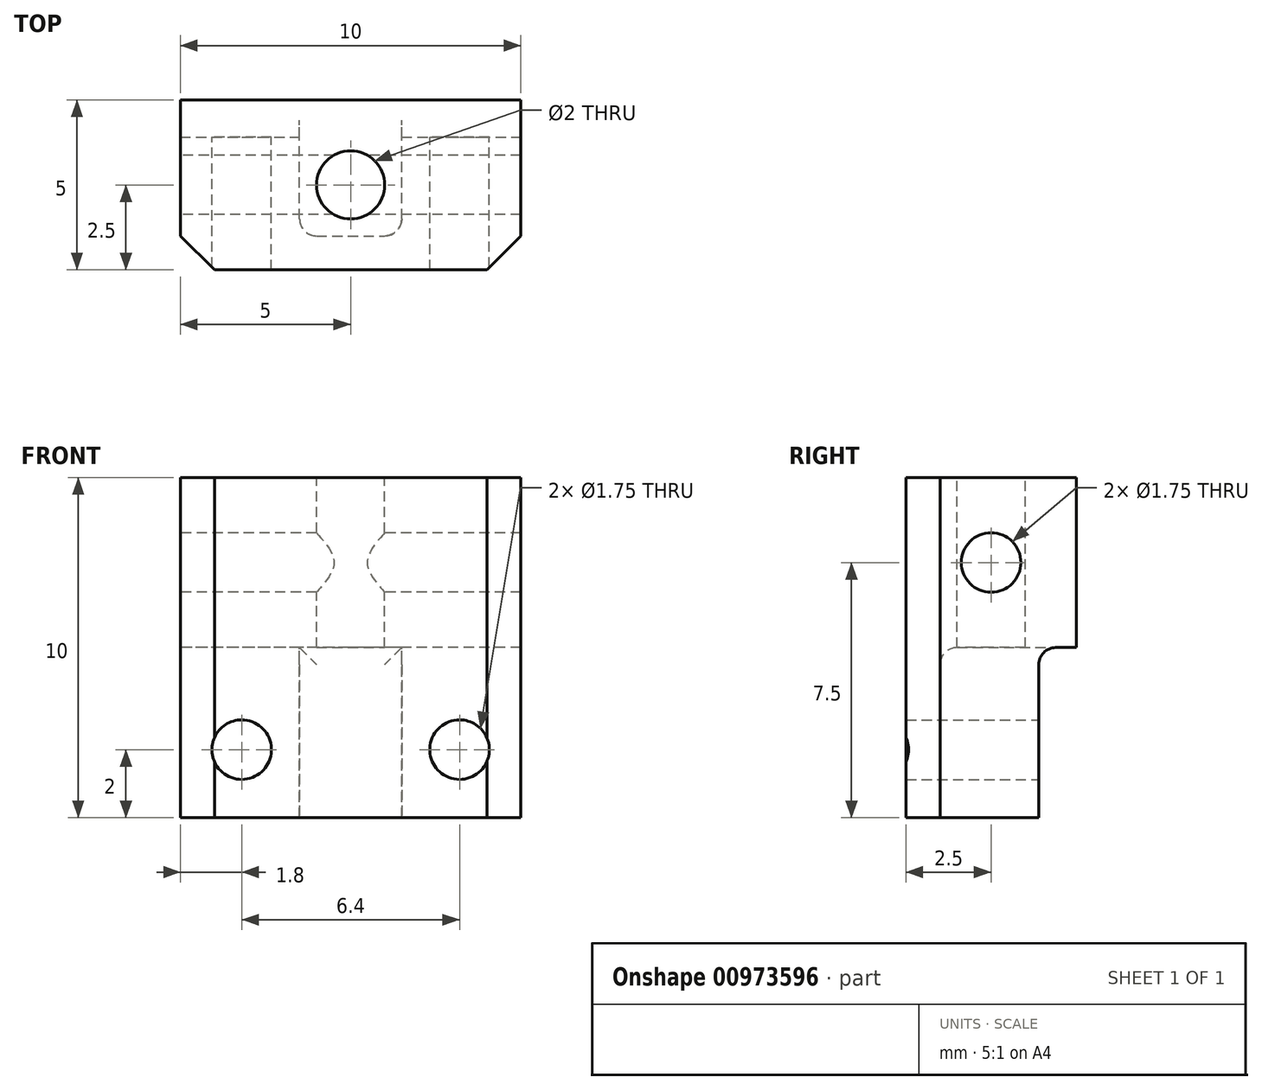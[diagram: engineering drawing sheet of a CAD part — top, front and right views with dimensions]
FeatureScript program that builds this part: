
annotation { "Feature Type Name" : "Feature", "Feature Type Description" : "" }
export const myFeature = defineFeature(function(context is Context, id is Id, definition is map)
    precondition{}
    {
        {
            var Q0;
            Q0=qCreatedBy(makeId("Top.planeOp"),FACE);
            var sketch = newSketch(context, id + "F0", { "sketchPlane" : qUnion([Q0])});
            skLineSegment(sketch, "E0.bottom", {"start": v(-5, 2.5) * mm, "end": v(5, 2.5) * mm});
            skLineSegment(sketch, "E0.top", {"start": v(-5, -2.5) * mm, "end": v(5, -2.5) * mm});
            skLineSegment(sketch, "E0.left", {"start": v(-5, 2.5) * mm, "end": v(-5, -2.5) * mm});
            skLineSegment(sketch, "E0.right", {"start": v(5, 2.5) * mm, "end": v(5, -2.5) * mm});
            skLineSegment(sketch, "E1", {"start": v(0, 65.84) * mm, "end": v(0, -65.84) * mm, "construction": true});
            skLineSegment(sketch, "E2", {"start": v(-87.05, 0) * mm, "end": v(87.05, 0) * mm, "construction": true});
            skSolve(sketch);
        }
        {
            var Q0;
            Q0 = qSketchRegion(id + "F0", true);
            extrude(context, id + "F1", {"entities" : qUnion([Q0]), "depth" : 10 * mm, "offsetDistance" : 25 * mm});
        }
        {
            var Q0;
            Q0=makeQuery(id+"F1.opExtrude","SWEPT_FACE",FACE,{"disambiguationData":[OSD([sQuery(id+"F0.wireOp",EDGE,"E0.bottom")])]});
            var sketch = newSketch(context, id + "F2", { "sketchPlane" : qUnion([Q0])});
            skLineSegment(sketch, "E3.bottom", {"start": v(-1.5, 0) * mm, "end": v(1.5, 0) * mm});
            skLineSegment(sketch, "E3.top", {"start": v(-1.5, 5) * mm, "end": v(1.5, 5) * mm});
            skLineSegment(sketch, "E3.left", {"start": v(-1.5, 0) * mm, "end": v(-1.5, 5) * mm});
            skLineSegment(sketch, "E3.right", {"start": v(1.5, 0) * mm, "end": v(1.5, 5) * mm});
            skLineSegment(sketch, "E4", {"start": v(0, -0.33) * mm, "end": v(0, 10.8) * mm, "construction": true});
            skSolve(sketch);
        }
        {
            var Q0;
            Q0 = qSketchRegion(id + "F2", true);
            extrude(context, id + "F3", {"entities" : qUnion([Q0]), "operationType" : NewBodyOperationType.REMOVE, "oppositeDirection" : true, "depth" : 4 * mm, "offsetDistance" : 25 * mm});
        }
        {
            var Q0;
            Q0=makeQuery(id+"F1.opExtrude","SWEPT_FACE",FACE,{"disambiguationData":[OSD([sQuery(id+"F0.wireOp",EDGE,"E0.bottom")])]});
            var sketch = newSketch(context, id + "F4", { "sketchPlane" : qUnion([Q0])});
            skLineSegment(sketch, "E5.bottom", {"start": v(-5, 0) * mm, "end": v(5, 0) * mm});
            skLineSegment(sketch, "E5.top", {"start": v(-5, 5) * mm, "end": v(5, 5) * mm});
            skLineSegment(sketch, "E5.left", {"start": v(-5, 0) * mm, "end": v(-5, 5) * mm});
            skLineSegment(sketch, "E5.right", {"start": v(5, 0) * mm, "end": v(5, 5) * mm});
            skSolve(sketch);
        }
        {
            var Q0;
            Q0 = qSketchRegion(id + "F4", true);
            extrude(context, id + "F5", {"entities" : qUnion([Q0]), "operationType" : NewBodyOperationType.REMOVE, "oppositeDirection" : true, "depth" : 1.1 * mm, "offsetDistance" : 25 * mm});
        }
        {
            var Q0;
            Q0=makeQuery(id+"F3.boolean.opBoolean","COPY",EDGE,{"derivedFrom":makeQuery(id+"F3.opExtrude","CAP_EDGE",EDGE,{"disambiguationData":[OSD([sQuery(id+"F2.wireOp",EDGE,"E3.left")])],"isStart":false})});
            var Q1;
            Q1=makeQuery(id+"F3.boolean.opBoolean","COPY",EDGE,{"derivedFrom":makeQuery(id+"F3.opExtrude","CAP_EDGE",EDGE,{"disambiguationData":[OSD([sQuery(id+"F2.wireOp",EDGE,"E3.right")])],"isStart":false})});
            var Q2;
            Q2=makeQuery(id+"F3.boolean.opBoolean","COPY",EDGE,{"derivedFrom":makeQuery(id+"F3.opExtrude","CAP_EDGE",EDGE,{"disambiguationData":[OSD([sQuery(id+"F2.wireOp",EDGE,"E3.top")])],"isStart":false})});
            fillet(context, id + "F6", {"entities" : qUnion([Q0, Q1, Q2]), "radius" : 0.5 * mm, "tangentPropagation" : true, "allowEdgeOverflow" : false});
        }
        {
            var Q0;
            {var subQ0=sQuery(id+"F4.wireOp",EDGE,"E5.top");Q0=makeQuery(id+"F5.boolean.opBoolean","COPY",EDGE,{"disambiguationData":[TD([makeQuery(id+"F1.opExtrude","SWEPT_FACE",FACE,{"disambiguationData":[OSD([sQuery(id+"F0.wireOp",EDGE,"E0.left")])]})])],"derivedFrom":makeQuery(id+"F5.opExtrude","CAP_EDGE",EDGE,{"disambiguationData":[OSD([subQ0])],"isStart":false})});}
            var Q1;
            {var subQ0=sQuery(id+"F4.wireOp",EDGE,"E5.top");Q1=makeQuery(id+"F5.boolean.opBoolean","COPY",EDGE,{"disambiguationData":[TD([makeQuery(id+"F1.opExtrude","SWEPT_FACE",FACE,{"disambiguationData":[OSD([sQuery(id+"F0.wireOp",EDGE,"E0.right")])]})])],"derivedFrom":makeQuery(id+"F5.opExtrude","CAP_EDGE",EDGE,{"disambiguationData":[OSD([subQ0])],"isStart":false})});}
            fillet(context, id + "F7", {"entities" : qUnion([Q0, Q1]), "radius" : 0.5 * mm, "tangentPropagation" : true, "allowEdgeOverflow" : false});
        }
        {
            var Q0;
            Q0=makeQuery(id+"F1.opExtrude","SWEPT_EDGE",EDGE,{"disambiguationData":[OSD([sQuery(id+"F0.wireOp",EDGE,"E0.top"),sQuery(id+"F0.wireOp",EDGE,"E0.right")])]});
            var Q1;
            Q1=makeQuery(id+"F1.opExtrude","SWEPT_EDGE",EDGE,{"disambiguationData":[OSD([sQuery(id+"F0.wireOp",EDGE,"E0.top"),sQuery(id+"F0.wireOp",EDGE,"E0.left")])]});
            chamfer(context, id + "F8", {"entities" : qUnion([Q0, Q1]), "width" : 1 * mm, "tangentPropagation" : true});
        }
        {
            var Q0;
            {var subQ0=sQuery(id+"F0.wireOp",EDGE,"E0.left");var subQ1=sQuery(id+"F4.wireOp",EDGE,"E5.top");Q0=makeQuery(id+"F5.boolean.opBoolean","COPY",FACE,{"disambiguationData":[TD([makeQuery(id+"F1.opExtrude","SWEPT_FACE",FACE,{"disambiguationData":[OSD([subQ0])]})])],"derivedFrom":makeQuery(id+"F5.opExtrude","CAP_FACE",FACE,{"disambiguationData":[OSD([sQuery(id+"F4.wireOp",EDGE,"E5.bottom"),subQ1,sQuery(id+"F4.wireOp",EDGE,"E5.left"),sQuery(id+"F4.wireOp",EDGE,"E5.right")])],"isStart":false})});}
            var sketch = newSketch(context, id + "F9", { "sketchPlane" : qUnion([Q0])});
            skPoint(sketch, "E6", {"position": v(-3.2, 2) * mm});
            skPoint(sketch, "E7", {"position": v(3.2, 2) * mm});
            skSolve(sketch);
        }
        {
            var Q0;
            Q0=sQuery(id+"F9.wireOp",VERTEX,"E6");
            var Q1;
            Q1=sQuery(id+"F9.wireOp",VERTEX,"E7");
            var Q2;
            Q2=makeQuery(id+"F1.opExtrude","SWEPT_BODY",BODY,{"disambiguationData":[OSD([sQuery(id+"F0.wireOp",EDGE,"E0.bottom"),sQuery(id+"F0.wireOp",EDGE,"E0.top"),sQuery(id+"F0.wireOp",EDGE,"E0.left"),sQuery(id+"F0.wireOp",EDGE,"E0.right"),sQuery(id+"F0.wireOp",EDGE,"H4gdiPJo-8vIM-zMkF-eMMu-KdfANKpb1p3E")])]});
            hole(context, id + "F10", {"style" : HoleStyle.SIMPLE, "endStyle" : HoleEndStyle.THROUGH, "standardTappedOrClearance" : lookupTablePath({ "standard" : "ISO", "engagement" : "75%", "pitch" : "0.25 mm", "size" : "M2", "type" : "Tapped" }), "standardBlindInLast" : lookupTablePath({ "standard" : "ISO", "fit" : "Normal", "engagement" : "75%", "pitch" : "0.25 mm", "size" : "M2", "type" : "Clearance & tapped" }), "holeDiameter" : 1.75 * mm, "majorDiameter" : 2 * mm, "showTappedDepth" : true, "isTappedThrough" : true, "tappedDepth" : 12 * mm, "tapClearance" : 3, "locations" : qUnion([Q0, Q1]), "scope" : qUnion([Q2])});
        }
        {
            var Q0;
            Q0=makeQuery(id+"F1.opExtrude","SWEPT_FACE",FACE,{"disambiguationData":[OSD([sQuery(id+"F0.wireOp",EDGE,"E0.left")])]});
            var sketch = newSketch(context, id + "F11", { "sketchPlane" : qUnion([Q0])});
            skPoint(sketch, "E8", {"position": v(0, 7.5) * mm});
            skSolve(sketch);
        }
        {
            var Q0;
            Q0=sQuery(id+"F11.wireOp",VERTEX,"E8");
            var Q1;
            Q1=makeQuery(id+"F1.opExtrude","SWEPT_BODY",BODY,{"disambiguationData":[OSD([sQuery(id+"F0.wireOp",EDGE,"E0.bottom"),sQuery(id+"F0.wireOp",EDGE,"E0.top"),sQuery(id+"F0.wireOp",EDGE,"E0.left"),sQuery(id+"F0.wireOp",EDGE,"E0.right"),sQuery(id+"F0.wireOp",EDGE,"H4gdiPJo-8vIM-zMkF-eMMu-KdfANKpb1p3E")])]});
            hole(context, id + "F12", {"style" : HoleStyle.SIMPLE, "endStyle" : HoleEndStyle.THROUGH, "standardTappedOrClearance" : lookupTablePath({ "standard" : "ISO", "engagement" : "75%", "pitch" : "0.25 mm", "size" : "M2", "type" : "Tapped" }), "standardBlindInLast" : lookupTablePath({ "standard" : "ISO", "fit" : "Normal", "engagement" : "75%", "pitch" : "0.25 mm", "size" : "M2", "type" : "Clearance & tapped" }), "holeDiameter" : 1.75 * mm, "majorDiameter" : 2 * mm, "showTappedDepth" : true, "isTappedThrough" : true, "tappedDepth" : 12 * mm, "tapClearance" : 3, "locations" : qUnion([Q0]), "scope" : qUnion([Q1])});
        }
        {
            var Q0;
            Q0=makeQuery(id+"F1.opExtrude","CAP_FACE",FACE,{"disambiguationData":[OSD([sQuery(id+"F0.wireOp",EDGE,"E0.bottom"),sQuery(id+"F0.wireOp",EDGE,"E0.top"),sQuery(id+"F0.wireOp",EDGE,"E0.left"),sQuery(id+"F0.wireOp",EDGE,"E0.right")])],"isStart":false});
            var sketch = newSketch(context, id + "F13", { "sketchPlane" : qUnion([Q0])});
            skPoint(sketch, "E9", {"position": v(0, 0) * mm});
            skLineSegment(sketch, "E10", {"start": v(0, 4.4) * mm, "end": v(0, -3.34) * mm, "construction": true});
            skLineSegment(sketch, "E11", {"start": v(-6.6, 0) * mm, "end": v(8.03, 0) * mm, "construction": true});
            skSolve(sketch);
        }
        {
            var Q0;
            Q0=sQuery(id+"F13.wireOp",VERTEX,"E9");
            var Q1;
            Q1=makeQuery(id+"F1.opExtrude","SWEPT_BODY",BODY,{"disambiguationData":[OSD([sQuery(id+"F0.wireOp",EDGE,"E0.bottom"),sQuery(id+"F0.wireOp",EDGE,"E0.top"),sQuery(id+"F0.wireOp",EDGE,"E0.left"),sQuery(id+"F0.wireOp",EDGE,"E0.right")])]});
            hole(context, id + "F14", {"style" : HoleStyle.SIMPLE, "endStyle" : HoleEndStyle.THROUGH, "holeDiameter" : 2 * mm, "majorDiameter" : 2 * mm, "isTappedThrough" : true, "tappedDepth" : 12 * mm, "tapClearance" : 3, "locations" : qUnion([Q0]), "scope" : qUnion([Q1])});
        }
    });
